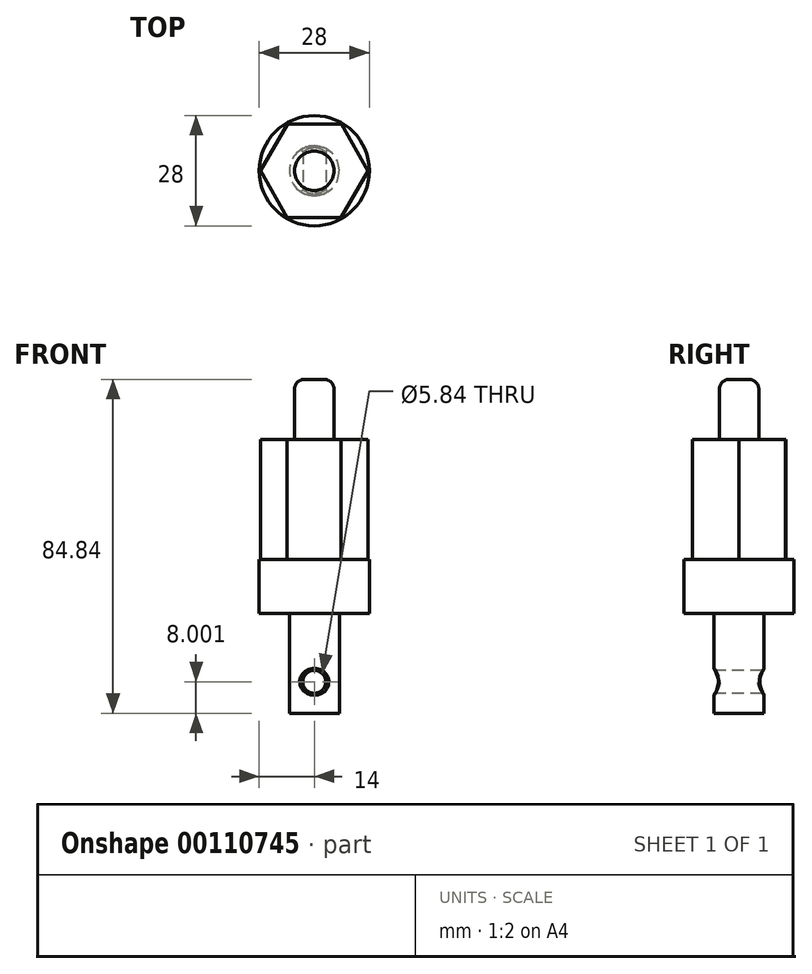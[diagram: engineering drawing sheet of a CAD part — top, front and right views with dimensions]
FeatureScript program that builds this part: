
annotation { "Feature Type Name" : "Feature", "Feature Type Description" : "" }
export const myFeature = defineFeature(function(context is Context, id is Id, definition is map)
    precondition{}
    {
        {
            var Q0;
            Q0=qCreatedBy(makeId("Top.planeOp"),FACE);
            var sketch = newSketch(context, id + "F0", { "sketchPlane" : qUnion([Q0])});
            skCircle(sketch, "E0", {"center": v(0, 0) * mm, "radius": 6.35 * mm});
            skSolve(sketch);
        }
        {
            var Q0;
            Q0 = qSketchRegion(id + "F0", true);
            extrude(context, id + "F1", {"entities" : qUnion([Q0]), "depth" : 25.4 * mm});
        }
        {
            var Q0;
            Q0=qCreatedBy(makeId("Front.planeOp"),FACE);
            var sketch = newSketch(context, id + "F2", { "sketchPlane" : qUnion([Q0])});
            skCircle(sketch, "E1", {"center": v(0, 8) * mm, "radius": 2.92 * mm});
            skSolve(sketch);
        }
        {
            var Q0;
            Q0 = qSketchRegion(id + "F2", true);
            extrude(context, id + "F3", {"entities" : qUnion([Q0]), "operationType" : NewBodyOperationType.REMOVE, "endBound" : BoundingType.THROUGH_ALL, "oppositeDirection" : true, "depth" : 25.4 * mm, "hasSecondDirection" : true, "secondDirectionBound" : SecondDirectionBoundingType.THROUGH_ALL, "secondDirectionOppositeDirection" : false, "secondDirectionDepth" : 25.4 * mm});
        }
        {
            var Q0;
            Q0=makeQuery(id+"F3.boolean.opBoolean","INTERSECT",EDGE,{"disambiguationData":[OD(0.0)],"derivedFrom":[makeQuery(id+"F1.opExtrude","SWEPT_FACE",FACE,{"disambiguationData":[OSD([sQuery(id+"F0.wireOp",EDGE,"E0")])]}),makeQuery(id+"F3.opExtrude","SWEPT_FACE",FACE,{"disambiguationData":[OSD([sQuery(id+"F2.wireOp",EDGE,"E1")])]})]});
            var Q1;
            Q1=makeQuery(id+"F3.boolean.opBoolean","INTERSECT",EDGE,{"disambiguationData":[OD(1.0)],"derivedFrom":[makeQuery(id+"F1.opExtrude","SWEPT_FACE",FACE,{"disambiguationData":[OSD([sQuery(id+"F0.wireOp",EDGE,"E0")])]}),makeQuery(id+"F3.opExtrude","SWEPT_FACE",FACE,{"disambiguationData":[OSD([sQuery(id+"F2.wireOp",EDGE,"E1")])]})]});
            fillet(context, id + "F4", {"entities" : qUnion([Q0, Q1]), "radius" : 0.5 * mm, "tangentPropagation" : true, "allowEdgeOverflow" : false});
        }
        {
            var Q0;
            Q0=makeQuery(id+"F1.opExtrude","CAP_FACE",FACE,{"disambiguationData":[OSD([sQuery(id+"F0.wireOp",EDGE,"E0")])],"isStart":false});
            var sketch = newSketch(context, id + "F5", { "sketchPlane" : qUnion([Q0])});
            skCircle(sketch, "E2", {"center": v(0, 0) * mm, "radius": 14 * mm});
            skSolve(sketch);
        }
        {
            var Q0;
            Q0 = qSketchRegion(id + "F5", true);
            extrude(context, id + "F6", {"entities" : qUnion([Q0]), "depth" : 13.72 * mm});
        }
        {
            var Q0;
            Q0=makeQuery(id+"F6.opExtrude","CAP_FACE",FACE,{"disambiguationData":[OSD([sQuery(id+"F5.wireOp",EDGE,"E2")])],"isStart":false});
            var sketch = newSketch(context, id + "F7", { "sketchPlane" : qUnion([Q0])});
            skCircle(sketch, "E3.cCircle", {"center": v(0, 0) * mm, "radius": 11.86 * mm, "construction": true});
            skLineSegment(sketch, "E3.0", {"start": v(-13.7, 0.05) * mm, "end": v(-6.8, 11.88) * mm});
            skLineSegment(sketch, "E3.1", {"start": v(-6.8, 11.88) * mm, "end": v(6.9, 11.83) * mm});
            skLineSegment(sketch, "E3.2", {"start": v(6.9, 11.83) * mm, "end": v(13.7, -0.05) * mm});
            skLineSegment(sketch, "E3.3", {"start": v(13.7, -0.05) * mm, "end": v(6.8, -11.88) * mm});
            skLineSegment(sketch, "E3.4", {"start": v(6.8, -11.88) * mm, "end": v(-6.9, -11.83) * mm});
            skLineSegment(sketch, "E3.5", {"start": v(-6.9, -11.83) * mm, "end": v(-13.7, 0.05) * mm});
            skPoint(sketch, "E3.0.midPoint", {"position": v(-10.24, 5.97) * mm});
            skSolve(sketch);
        }
        {
            var Q0;
            Q0 = qSketchRegion(id + "F7", true);
            extrude(context, id + "F8", {"entities" : qUnion([Q0]), "operationType" : NewBodyOperationType.ADD, "depth" : 30.48 * mm});
        }
        {
            var Q0;
            Q0=makeQuery(id+"F8.opExtrude","CAP_FACE",FACE,{"disambiguationData":[OSD([sQuery(id+"F7.wireOp",EDGE,"E3.0"),sQuery(id+"F7.wireOp",EDGE,"E3.1"),sQuery(id+"F7.wireOp",EDGE,"E3.2"),sQuery(id+"F7.wireOp",EDGE,"E3.3"),sQuery(id+"F7.wireOp",EDGE,"E3.4"),sQuery(id+"F7.wireOp",EDGE,"E3.5")])],"isStart":false});
            var sketch = newSketch(context, id + "F9", { "sketchPlane" : qUnion([Q0])});
            skCircle(sketch, "E4", {"center": v(0, 0) * mm, "radius": 5.02 * mm});
            skSolve(sketch);
        }
        {
            var Q0;
            Q0 = qSketchRegion(id + "F9", true);
            extrude(context, id + "F10", {"entities" : qUnion([Q0]), "operationType" : NewBodyOperationType.ADD, "depth" : 15.24 * mm});
        }
        {
            var Q0;
            Q0=makeQuery(id+"F10.opExtrude","CAP_EDGE",EDGE,{"disambiguationData":[OSD([sQuery(id+"F9.wireOp",EDGE,"E4")])],"isStart":false});
            var Q1;
            Q1=makeQuery(id+"F10.opExtrude","CAP_EDGE",EDGE,{"disambiguationData":[OSD([sQuery(id+"F9.wireOp",EDGE,"E4")])],"isStart":true});
            fillet(context, id + "F11", {"entities" : qUnion([Q0, Q1]), "radius" : 2.54 * mm, "tangentPropagation" : true, "allowEdgeOverflow" : false});
        }
    });
